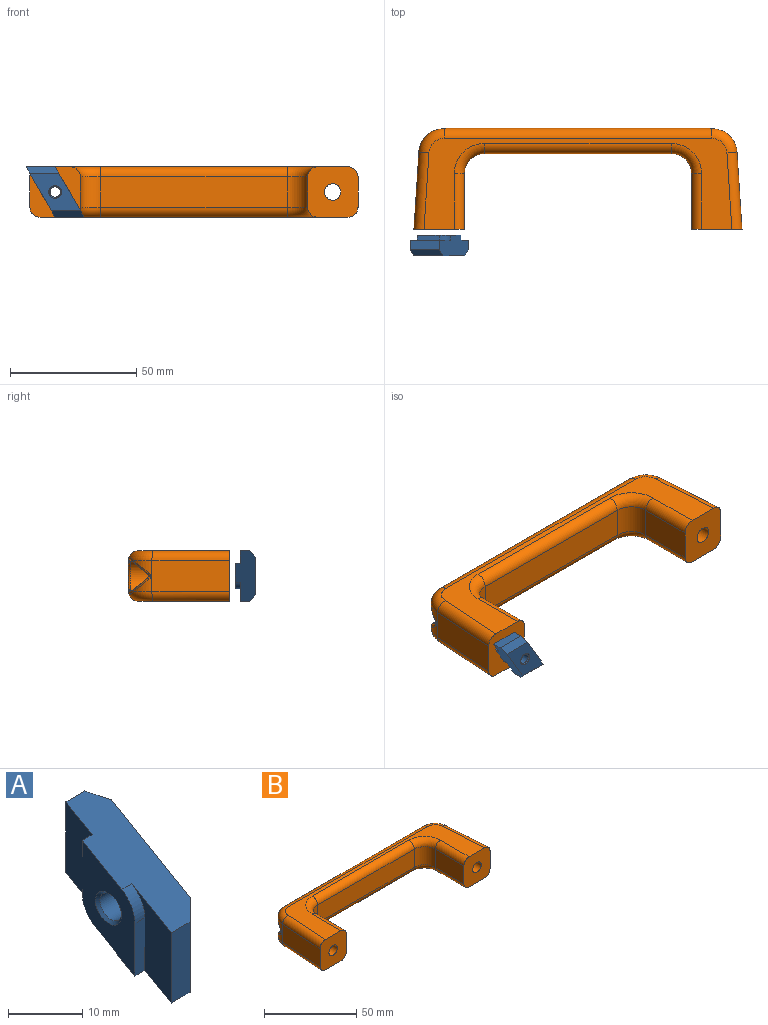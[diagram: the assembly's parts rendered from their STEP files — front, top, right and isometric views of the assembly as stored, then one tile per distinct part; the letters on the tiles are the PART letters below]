
ASSEMBLY  parts=2 mates=1
PART A: 17 faces, bbox 8x20x23.1 mm
  f0: plane 15.88x7.5mm, normal (-1,0,0), area 59.1mm2, adj f2,f7,f8,f10,f11
  f1: plane 15.88x7.5mm, normal (-1,0,0), area 59.1mm2, adj f6,f7,f8,f9,f12
  f2: plane 11.55x3.6mm, normal (0,-1,0), area 41.6mm2, adj f0,f3,f7,f8
  f3: plane 12.99x2.5mm, normal (0.71,-0.71,0), area 40.8mm2, adj f2,f4,f7,f8
  f4: plane 20.21x15mm, normal (1,0,0), area 153.6mm2, adj f3,f5,f7,f8,f14
  f5: plane 12.99x2.5mm, normal (0.71,0.71,0), area 40.8mm2, adj f4,f6,f7,f8
  f6: plane 11.55x3.6mm, normal (0,1,0), area 41.6mm2, adj f1,f5,f7,f8
  f7: plane 20x11.55mm, normal (0,-0.5,0.87), area 150.1mm2, adj f0,f1,f2,f3,f4,f5,f6,f9
  f8: plane 20x11.55mm, normal (0,0.5,-0.87), area 150.1mm2, adj f0,f1,f2,f3,f4,f5,f6,f11
  f9: plane 8.66x1.9mm, normal (0,1,0), area 16.5mm2, adj f1,f7,f12,f13
  f10: cylinder r=5mm len=4.33mm, axis (1,0,0), area 9.9mm2, adj f0,f7,f11,f13
  f11: plane 8.66x1.9mm, normal (0,-1,0), area 16.5mm2, adj f0,f8,f10,f13
  f12: cylinder r=5mm len=4.33mm, axis (1,0,0), area 9.9mm2, adj f1,f8,f9,f13
  f13: plane 17.32x10mm, normal (-1,0,0), area 93.1mm2, adj f7,f8,f9,f10,f11,f12,f16
  f14: cone r=2.5mm half-angle=45deg, axis (1,0,0), area 8.8mm2, adj f4,f15
  f15: cylinder r=2.07mm len=7.13mm, axis (-1,0,0), area 92.7mm2, adj f14,f16
  f16: cone r=2.07mm half-angle=45deg, axis (-1,0,0), area 8.8mm2, adj f13,f15
PART B: 58 faces, bbox 130.1x52.8x20.1 mm
  f0: bspline ~21.59x5.29mm, area 3.3mm2, adj f1,f3,f13,f30
  f1: bspline ~21.59x5.3mm, area 3.3mm2, adj f0,f2,f3,f13
  f2: bspline ~11.05x7.4mm, area 18.8mm2, adj f1,f3,f13,f32
  f3: cylinder r=10mm len=12mm, axis (0,0,-1), area 47.2mm2, adj f0,f1,f2,f7,f16,f25,f30
  f4: plane 102.79x12mm, normal (0,1,0), area 1175.8mm2, adj f17,f24,f29,f54
  f5: plane 22x12mm, normal (-1,0,0), area 264mm2, adj f6,f9,f18,f23
  f6: plane 20.11x20.11mm, normal (0,-1,0), area 353.1mm2, adj f5,f7,f10,f11,f12,f15,f18,f23
  f7: plane 30.65x12mm, normal (1,0.06,0), area 368.5mm2, adj f3,f6,f15,f26
  f8: plane 74x12mm, normal (0,-1,0), area 888mm2, adj f9,f20,f21,f40
  f9: cylinder r=8mm len=12mm, axis (0,0,-1), area 150.8mm2, adj f5,f8,f19,f22
  f10: plane 121.98x36mm, normal (0,0,1), area 1024.1mm2, adj f6,f21,f22,f23,f24,f25,f26,f38
  f11: plane 121.98x36mm, normal (0,0,-1), area 1024.1mm2, adj f6,f15,f16,f17,f18,f19,f20,f38
  f12: cylinder r=3.25mm len=23mm, axis (0,-1,0), area 469.7mm2, adj f6,f14
  f13: cylinder r=6mm len=16mm, axis (0,-1,0), area 529mm2, adj f0,f1,f2,f14,f27,f28,f29,f30
  f14: plane 12x12mm, normal (0,1,0), area 79.9mm2, adj f12,f13
  f15: cylinder r=4mm len=30.9mm, axis (-0.06,1,0), area 192.1mm2, adj f6,f7,f11,f16
  f16: torus R=6mm, axis (0,0,1), area 74.2mm2, adj f3,f11,f15,f17,f32
  f17: cylinder r=4mm len=106.08mm, axis (-1,0,0), area 664.9mm2, adj f4,f11,f16,f31,f45,f56
  f18: cylinder r=4mm len=22mm, axis (0,-1,0), area 138.2mm2, adj f5,f6,f11,f19
  f19: torus R=12mm, axis (0,0,1), area 93.3mm2, adj f9,f11,f18,f20
  f20: cylinder r=4mm len=74mm, axis (1,0,0), area 465mm2, adj f8,f11,f19,f47
  f21: cylinder r=4mm len=74mm, axis (-1,0,0), area 465mm2, adj f8,f10,f22,f48
  f22: torus R=12mm, axis (0,0,1), area 93.3mm2, adj f9,f10,f21,f23
  f23: cylinder r=4mm len=22mm, axis (0,1,0), area 138.2mm2, adj f5,f6,f10,f22
  f24: cylinder r=4mm len=106.08mm, axis (1,0,0), area 664.9mm2, adj f4,f10,f25,f27,f50,f52
  f25: torus R=6mm, axis (0,0,1), area 74.2mm2, adj f3,f10,f24,f26,f28
  f26: cylinder r=4mm len=30.9mm, axis (0.06,-1,0), area 192.1mm2, adj f6,f7,f10,f25
  f27: bspline ~2.86x2.18mm, area 2.9mm2, adj f13,f24,f28,f29
  f28: bspline ~8.22x3.98mm, area 11.6mm2, adj f13,f25,f27,f30
  f29: torus R=7mm, axis (0,1,0), area 20.6mm2, adj f4,f13,f27,f31
  f30: bspline ~11.21x7.44mm, area 18.7mm2, adj f0,f3,f13,f28
  f31: bspline ~2.86x2.18mm, area 2.9mm2, adj f13,f17,f29,f32
  f32: bspline ~8.22x3.99mm, area 11.6mm2, adj f2,f13,f16,f31
  f33: bspline ~21.59x5.29mm, area 3.3mm2, adj f34,f36,f42,f55
  f34: bspline ~21.59x5.3mm, area 3.3mm2, adj f33,f35,f36,f42
  f35: bspline ~11.05x7.4mm, area 18.8mm2, adj f34,f36,f42,f57
  f36: cylinder r=10mm len=12mm, axis (0,0,-1), area 47.2mm2, adj f33,f34,f35,f39,f45,f50,f55
  f37: plane 22x12mm, normal (1,0,0), area 264mm2, adj f38,f40,f46,f49
  f38: plane 20.11x20.11mm, normal (0,-1,0), area 353.1mm2, adj f10,f11,f37,f39,f41,f44,f46,f49
  f39: plane 30.65x12mm, normal (-1,0.06,0), area 368.5mm2, adj f36,f38,f44,f51
  f40: cylinder r=8mm len=12mm, axis (0,0,-1), area 150.8mm2, adj f8,f37,f47,f48
  f41: cylinder r=3.25mm len=23mm, axis (0,-1,0), area 469.7mm2, adj f38,f43
  f42: cylinder r=6mm len=16mm, axis (0,-1,0), area 529mm2, adj f33,f34,f35,f43,f52,f53,f54,f55
  f43: plane 12x12mm, normal (0,1,0), area 79.9mm2, adj f41,f42
  f44: cylinder r=4mm len=30.9mm, axis (0.06,1,0), area 192.1mm2, adj f11,f38,f39,f45
  f45: torus R=6mm, axis (0,0,1), area 74.2mm2, adj f11,f17,f36,f44,f57
  f46: cylinder r=4mm len=22mm, axis (0,-1,0), area 138.2mm2, adj f11,f37,f38,f47
  f47: torus R=12mm, axis (0,0,1), area 93.3mm2, adj f11,f20,f40,f46
  f48: torus R=12mm, axis (0,0,1), area 93.3mm2, adj f10,f21,f40,f49
  f49: cylinder r=4mm len=22mm, axis (0,1,0), area 138.2mm2, adj f10,f37,f38,f48
  f50: torus R=6mm, axis (0,0,1), area 74.2mm2, adj f10,f24,f36,f51,f53
  f51: cylinder r=4mm len=30.9mm, axis (-0.06,-1,0), area 192.1mm2, adj f10,f38,f39,f50
  f52: bspline ~2.86x2.18mm, area 2.9mm2, adj f24,f42,f53,f54
  f53: bspline ~8.22x3.98mm, area 11.6mm2, adj f42,f50,f52,f55
  f54: torus R=7mm, axis (0,1,0), area 20.6mm2, adj f4,f42,f52,f56
  f55: bspline ~11.21x7.44mm, area 18.7mm2, adj f33,f36,f42,f53
  f56: bspline ~3x2.45mm, area 2.9mm2, adj f17,f42,f54,f57
  f57: bspline ~8.22x3.99mm, area 11.6mm2, adj f35,f42,f45,f56
PLACE A rot(axis=(-0.58,0.58,-0.58),120deg) t=(-54.72,-23.71,1.39)mm
PLACE B t=(0.28,-2.48,1.39)mm
MATE planar A.f14 <-> B.f54  axis (0,1,0) through (-54.72,-29.37,1.39)mm
